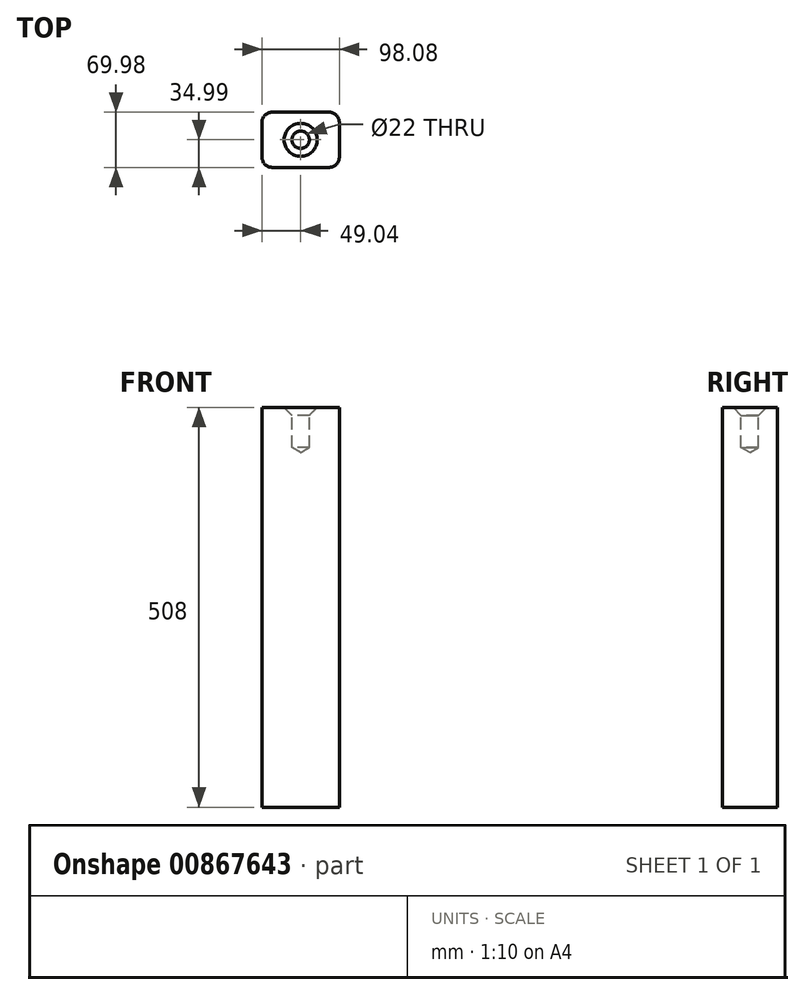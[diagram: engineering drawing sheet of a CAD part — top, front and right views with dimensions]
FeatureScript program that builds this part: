
annotation { "Feature Type Name" : "Feature", "Feature Type Description" : "" }
export const myFeature = defineFeature(function(context is Context, id is Id, definition is map)
    precondition{}
    {
        {
            var Q0;
            Q0=qCreatedBy(makeId("Top.planeOp"),FACE);
            var sketch = newSketch(context, id + "F0", { "sketchPlane" : qUnion([Q0])});
            skLineSegment(sketch, "E0.bottom", {"start": v(49.04, 34.99) * mm, "end": v(-49.04, 34.99) * mm});
            skLineSegment(sketch, "E0.top", {"start": v(49.04, -34.99) * mm, "end": v(-49.04, -34.99) * mm});
            skLineSegment(sketch, "E0.left", {"start": v(49.04, 34.99) * mm, "end": v(49.04, -34.99) * mm});
            skLineSegment(sketch, "E0.right", {"start": v(-49.04, 34.99) * mm, "end": v(-49.04, -34.99) * mm});
            skPoint(sketch, "E0.middle", {"position": v(0, 0) * mm});
            skSolve(sketch);
        }
        {
            var Q0;
            Q0=makeQuery(id+"F0.imprint","IMPRINT",FACE,{"disambiguationData":[TD([[makeQuery(id+"F0.imprint","IMPRINT",EDGE,{"derivedFrom":sQuery(id+"F0.wireOp",EDGE,"E0.bottom")}),1.0]])]});
            extrude(context, id + "F1", {"entities" : qUnion([Q0]), "depth" : 508 * mm, "offsetDistance" : 25.4 * mm});
        }
        {
            var Q0;
            Q0=makeQuery(id+"F1.opExtrude","SWEPT_EDGE",EDGE,{"disambiguationData":[OSD([sQuery(id+"F0.wireOp",EDGE,"E0.bottom"),sQuery(id+"F0.wireOp",EDGE,"E0.left")])]});
            var Q1;
            Q1=makeQuery(id+"F1.opExtrude","SWEPT_EDGE",EDGE,{"disambiguationData":[OSD([sQuery(id+"F0.wireOp",EDGE,"E0.bottom"),sQuery(id+"F0.wireOp",EDGE,"E0.right")])]});
            var Q2;
            Q2=makeQuery(id+"F1.opExtrude","SWEPT_EDGE",EDGE,{"disambiguationData":[OSD([sQuery(id+"F0.wireOp",EDGE,"E0.top"),sQuery(id+"F0.wireOp",EDGE,"E0.right")])]});
            var Q3;
            Q3=makeQuery(id+"F1.opExtrude","SWEPT_EDGE",EDGE,{"disambiguationData":[OSD([sQuery(id+"F0.wireOp",EDGE,"E0.top"),sQuery(id+"F0.wireOp",EDGE,"E0.left")])]});
            fillet(context, id + "F2", {"entities" : qUnion([Q0, Q1, Q2, Q3]), "radius" : 12.7 * mm, "tangentPropagation" : true, "allowEdgeOverflow" : false});
        }
        {
            var Q0;
            Q0=makeQuery(id+"F1.opExtrude","CAP_FACE",FACE,{"disambiguationData":[OSD([sQuery(id+"F0.wireOp",EDGE,"E0.bottom"),sQuery(id+"F0.wireOp",EDGE,"E0.top"),sQuery(id+"F0.wireOp",EDGE,"E0.left"),sQuery(id+"F0.wireOp",EDGE,"E0.right")])],"isStart":false});
            var sketch = newSketch(context, id + "F3", { "sketchPlane" : qUnion([Q0])});
            skPoint(sketch, "E1", {"position": v(0, 0) * mm});
            skSolve(sketch);
        }
        {
            var Q0;
            Q0=sQuery(id+"F3.wireOp",VERTEX,"E1");
            var Q1;
            Q1=makeQuery(id+"F1.opExtrude","SWEPT_BODY",BODY,{"disambiguationData":[OSD([sQuery(id+"F0.wireOp",EDGE,"E0.bottom"),sQuery(id+"F0.wireOp",EDGE,"E0.top"),sQuery(id+"F0.wireOp",EDGE,"E0.left"),sQuery(id+"F0.wireOp",EDGE,"E0.right")])]});
            hole(context, id + "F4", {"style" : HoleStyle.C_SINK, "endStyle" : HoleEndStyle.BLIND, "standardTappedOrClearance" : lookupTablePath({ "fit" : "Normal", "standard" : "ISO", "size" : "M20", "type" : "Clearance" }), "standardBlindInLast" : lookupTablePath({ "fit" : "Standard", "standard" : "ISO", "size" : "M20", "type" : "Clearance" }), "holeDiameter" : 22 * mm, "cSinkDiameter" : 42 * mm, "cSinkAngle" : 90 * degree, "majorDiameter" : 6.35 * mm, "holeDepth" : 50.8 * mm, "isTappedThrough" : true, "tappedDepth" : 12.7 * mm, "tapClearance" : 3, "locations" : qUnion([Q0]), "scope" : qUnion([Q1])});
        }
    });
